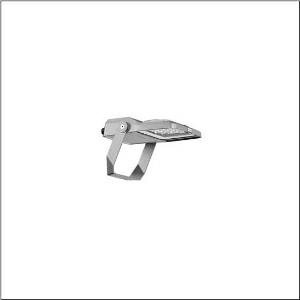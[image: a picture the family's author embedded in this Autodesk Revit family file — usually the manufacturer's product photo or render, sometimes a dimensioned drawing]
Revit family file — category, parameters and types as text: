
# Revit family: floodlight_fl_21_iq_micro___rs12_5xa7761a2b1a_22b8
name_source: partatom
category: Lighting Fixtures
units: mm (PartAtom-declared; Revit-internal decimal feet)

## family parameters
Cut with Voids When Loaded = No
Host = Face
Light Source = No
Part Type = Normal
Room Calculation Point = No
Round Connector Dimension = Use Diameter
Shared = No

## types (1)
- --- (1 x LED, 3090 lm, 23.1 W, 3000K)
    Apparent Load = 23 VA
    CIE Flux Codes = 79 92 99 100 100
    Color Rendering = 70
    Color Temperature = 3000K
    Default Elevation = 1800 mm
    Description = Floodlight FL 21 iQ micro, floodlight, primary light control with lens, of PMMA, primary optical cover: protective disc, of toughened safety glass, transparent, light distribution: RS12, light emission: direct distribution, installation type: surface-mounted, LED, High Power LED, rated luminous flux: 3.090lm, luminous efficacy: 134lm/W, light colour: 730, colour temperature: 3000K, control gear: iQ Comfort/DALI, control: optimised constant luminous flux control (CLO 2.0), Desk-Remote (wireless, voltage-free reading and setting of iQ features in the workshop via application-optimized NFC function/RFID function), Light-Fading, Smart-Wire, Night-Set, Lumen-Switch, Temp-Guard, Auto-Match, with terminal, 6-pole, mains connection: 220..240V, AC, 50/60Hz, start of lifetime: 23W, end of service life: 24W, reduction: 11W, luminaire housing, of diecast aluminium, powder-coated, Siteco® metallic grey (DB 702S), corrosivity category C5 mid according to DIN EN ISO 12944, suitable for swimming pools, chlorine-resistant, sealing non-destructively replaceable, mounting bracket, of steel, galvanised, powder-coated, Siteco® metallic grey (DB 702S), protection rating (complete): IP66, insulation class (complete): insulation class II (safety insulation), certification: CE, ENEC, VDE, protection symbol: D, impact resistance: IK07, permissible operating ambient temperature: -40..+40°C, permissible operating ambient temperature for outdoor applications: -40..+50°C, standard: DIN EN 12944, LABS conformity tested according to VDMA 24364:2018-05, packaging unit: 1 piece

Light Distribution: RS12
    Height = 65 mm
    Lamp = 1 x LED
    Lamp Light Flux = 3090 lm
    Lamp Power = 23.1 W
    Lamp count = 1
    Length = 312 mm
    Luminous efficacy = 134 lm/W
    Manufacturer = Siteco
    ModVariant = No
    Model = 5XA7761A2B1A
    Mounting Place = Wall
    Mounting Type = Surface mounted
    Number of Poles = 1
    OnlyDefault = Yes
    Power Factor = 1
    Product Name = Floodlight FL 21 iQ micro | RS12
    Product group = floodlight | wall mounted
    ProductGroupID = 2001
    Protection Class = Protection class II
    Protection Degree = IP 66
    RLX_Detail_Level = 1
    RLX_Emergency_Light_Flux = 0 lm
    RLX_Emergency_Type = 0
    RLX_Emergency_Type_DB = No
    RlxData = <blob elided: 74797 chars, md5=ef2c3482>
    Socket = socket
    Standby Power = 0 W
    System Light Flux = 3090 lm
    System Power = 23 W
    Type Comments = factory setting: luminous flux: 100 % | dim-lin: 254 | 455 mA
    Type Image = l_1006880.jpg
    URL = http://relux.com
    VarID = @adj_181930
    Voltage = 0 V
    Weight = 0.00 kg
    Width = 230 mm

## geometry (parser evidence)
native form markers: Blend x4, Sweep x11
no freeform markers — native parametric forms only
